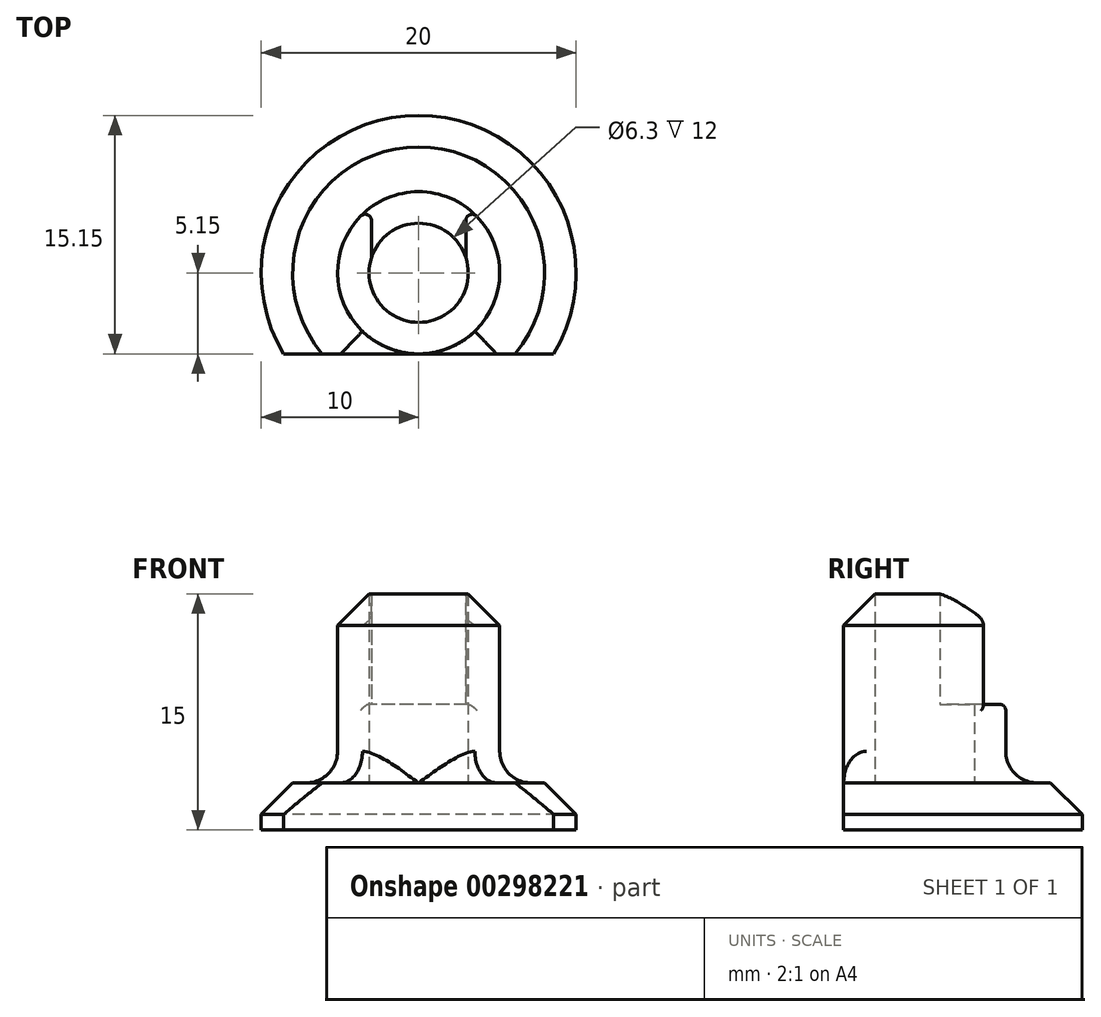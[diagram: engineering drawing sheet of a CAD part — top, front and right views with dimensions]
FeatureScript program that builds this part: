
annotation { "Feature Type Name" : "Feature", "Feature Type Description" : "" }
export const myFeature = defineFeature(function(context is Context, id is Id, definition is map)
    precondition{}
    {
        {
            var Q0;
            Q0=qCreatedBy(makeId("Top.planeOp"),FACE);
            var sketch = newSketch(context, id + "F0", { "sketchPlane" : qUnion([Q0])});
            skCircle(sketch, "E0", {"center": v(0, 0) * mm, "radius": 5.15 * mm});
            skCircle(sketch, "E1", {"center": v(0, 0) * mm, "radius": 3.15 * mm});
            skSolve(sketch);
        }
        {
            var Q0;
            Q0 = qSketchRegion(id + "F0", true);
            extrude(context, id + "F1", {"entities" : qUnion([Q0]), "depth" : 15 * mm});
        }
        {
            var Q0;
            Q0=qCreatedBy(makeId("Top.planeOp"),FACE);
            var sketch = newSketch(context, id + "F2", { "sketchPlane" : qUnion([Q0])});
            skLineSegment(sketch, "E2", {"start": v(-8.57, -5.15) * mm, "end": v(8.57, -5.15) * mm});
            skArc(sketch, "E3", {"start": v(8.57, -5.15) * mm, "mid": v(0, 10) * mm, "end": v(-8.57, -5.15) * mm});
            skSolve(sketch);
        }
        {
            var Q0;
            Q0 = qSketchRegion(id + "F2", true);
            extrude(context, id + "F3", {"entities" : qUnion([Q0]), "operationType" : NewBodyOperationType.ADD, "depth" : 3 * mm});
        }
        {
            var Q0;
            Q0=makeQuery(id+"F3.opExtrude","CAP_EDGE",EDGE,{"disambiguationData":[OSD([sQuery(id+"F2.wireOp",EDGE,"E3")])],"isStart":false});
            chamfer(context, id + "F4", {"entities" : qUnion([Q0]), "width" : 2 * mm, "tangentPropagation" : true});
        }
        {
            var Q0;
            Q0=makeQuery(id+"F3.boolean.opBoolean","INTERSECT",EDGE,{"derivedFrom":[makeQuery(id+"F1.opExtrude","SWEPT_FACE",FACE,{"disambiguationData":[OSD([sQuery(id+"F0.wireOp",EDGE,"E0")])]}),makeQuery(id+"F3.opExtrude","CAP_FACE",FACE,{"disambiguationData":[OSD([sQuery(id+"F2.wireOp",EDGE,"E2"),sQuery(id+"F2.wireOp",EDGE,"E3")])],"isStart":false})]});
            fillet(context, id + "F5", {"entities" : qUnion([Q0]), "radius" : 2 * mm, "tangentPropagation" : true, "allowEdgeOverflow" : false});
        }
        {
            var Q0;
            Q0=makeQuery(id+"F1.opExtrude","CAP_EDGE",EDGE,{"disambiguationData":[OSD([sQuery(id+"F0.wireOp",EDGE,"E0")])],"isStart":false});
            chamfer(context, id + "F6", {"entities" : qUnion([Q0]), "width" : 2 * mm, "tangentPropagation" : true});
        }
        {
            var Q0;
            Q0=qCreatedBy(makeId("Front.planeOp"),FACE);
            var sketch = newSketch(context, id + "F7", { "sketchPlane" : qUnion([Q0])});
            skLineSegment(sketch, "E4.bottom", {"start": v(3, 15) * mm, "end": v(-3, 15) * mm});
            skLineSegment(sketch, "E4.top", {"start": v(3, 8) * mm, "end": v(-3, 8) * mm});
            skLineSegment(sketch, "E4.left", {"start": v(3, 15) * mm, "end": v(3, 8) * mm});
            skLineSegment(sketch, "E4.right", {"start": v(-3, 15) * mm, "end": v(-3, 8) * mm});
            skSolve(sketch);
        }
        {
            var Q0;
            Q0 = qSketchRegion(id + "F7", true);
            extrude(context, id + "F8", {"entities" : qUnion([Q0]), "operationType" : NewBodyOperationType.REMOVE, "oppositeDirection" : true, "depth" : 10 * mm});
        }
        {
            var Q0;
            Q0=makeQuery(id+"F8.boolean.opBoolean","INTERSECT",EDGE,{"derivedFrom":[makeQuery(id+"F1.opExtrude","SWEPT_FACE",FACE,{"disambiguationData":[OSD([sQuery(id+"F0.wireOp",EDGE,"E0")])]}),makeQuery(id+"F8.opExtrude","SWEPT_FACE",FACE,{"disambiguationData":[OSD([sQuery(id+"F7.wireOp",EDGE,"E4.top")])]})]});
            var Q1;
            Q1=makeQuery(id+"F8.boolean.opBoolean","INTERSECT",EDGE,{"derivedFrom":[makeQuery(id+"F1.opExtrude","SWEPT_FACE",FACE,{"disambiguationData":[OSD([sQuery(id+"F0.wireOp",EDGE,"E0")])]}),makeQuery(id+"F8.opExtrude","SWEPT_FACE",FACE,{"disambiguationData":[OSD([sQuery(id+"F7.wireOp",EDGE,"E4.left")])]})]});
            var Q2;
            Q2=makeQuery(id+"F8.boolean.opBoolean","INTERSECT",EDGE,{"derivedFrom":[makeQuery(id+"F1.opExtrude","SWEPT_FACE",FACE,{"disambiguationData":[OSD([sQuery(id+"F0.wireOp",EDGE,"E0")])]}),makeQuery(id+"F8.opExtrude","SWEPT_FACE",FACE,{"disambiguationData":[OSD([sQuery(id+"F7.wireOp",EDGE,"E4.right")])]})]});
            fillet(context, id + "F9", {"entities" : qUnion([Q0, Q1, Q2]), "radius" : 0.4 * mm, "tangentPropagation" : true, "allowEdgeOverflow" : false});
        }
    });
